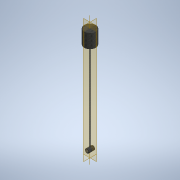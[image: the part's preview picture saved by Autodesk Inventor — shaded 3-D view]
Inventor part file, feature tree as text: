
AUTODESK INVENTOR PART (.ipt)
format: ipt  version: 2020 (Build 240168000, 168)  size: 131,584 bytes
history: native  units: in
note: dims shown in document units (in); Inventor stores cm internally (conversion verified against a paired STEP export)
features: extrude x3, sketch x3, hole x1
ambient origin geometry x8: Origin, YZ Plane, XZ Plane, XY Plane, X Axis, Y Axis, Z Axis, Center Point
bodies: Body1 (feature_tree)
feature tree (7):
  extrude  "Extrusion2"  Depth=7.0866in
  extrude  "Extrusion3"  Depth=9.8425in
  hole  "Hole1"  [1 undecoded]
  extrude  "Extrusion4"  Depth=155.9055in TaperAngle=0.0deg
  sketch  "Sketch6"  dims[d14=4.7244in d15=7.0866in]
  sketch  "Sketch7"  dims[d16=9.8425in d17=0.0in d18=1.9685in]
  sketch  "Sketch8"  dims[d19=21.2598in d20=0.0in d21=4.7244in d22=29.5276in d23=14.7638in d24=9.8425in d25=90.0deg d26=39.3701in d27=0.8108in d28=19.685in d29=23.622in d30=0.0in d31=155.9055in d32=155.9055in d33=0.0in]
note: 1 required parameter value undecoded (feature->parameter linkage not recoverable at this tier; creation-order binding heuristic only, values carry confidence <= 0.55)
